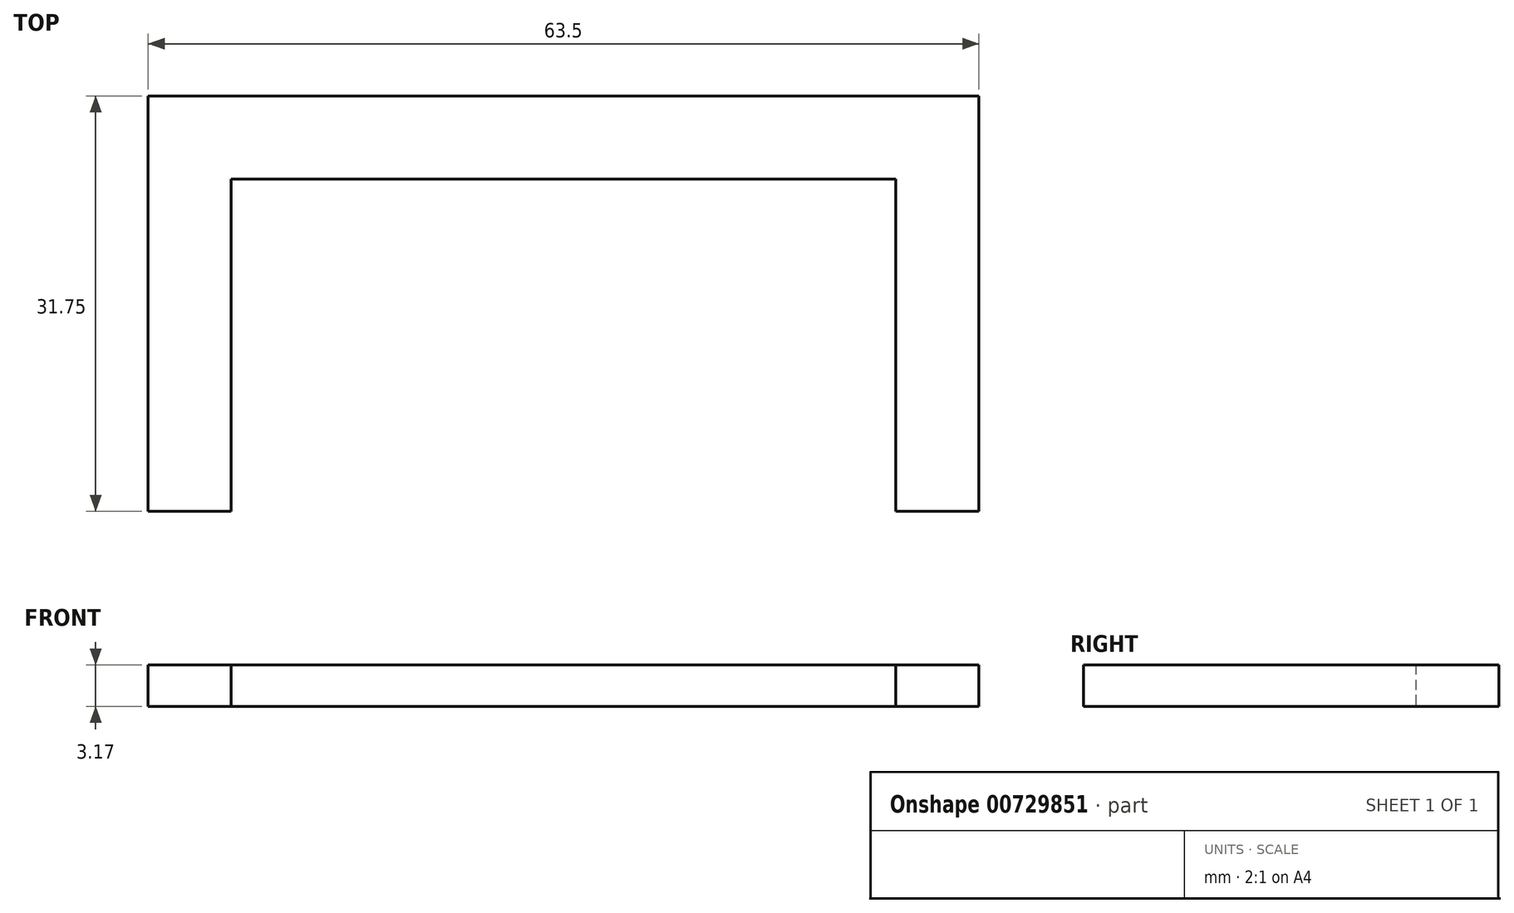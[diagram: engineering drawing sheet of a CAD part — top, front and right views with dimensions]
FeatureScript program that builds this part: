
annotation { "Feature Type Name" : "Feature", "Feature Type Description" : "" }
export const myFeature = defineFeature(function(context is Context, id is Id, definition is map)
    precondition{}
    {
        {
            var Q0;
            Q0=qCreatedBy(makeId("Top.planeOp"),FACE);
            var sketch = newSketch(context, id + "F0", { "sketchPlane" : qUnion([Q0])});
            skLineSegment(sketch, "E0", {"start": v(-85, -63.2) * mm, "end": v(-85, -31.44) * mm});
            skLineSegment(sketch, "E1", {"start": v(-85, -31.44) * mm, "end": v(-21.5, -31.44) * mm});
            skLineSegment(sketch, "E2", {"start": v(-21.5, -31.44) * mm, "end": v(-21.5, -63.2) * mm});
            skLineSegment(sketch, "E3", {"start": v(-78.65, -63.2) * mm, "end": v(-78.65, -37.8) * mm});
            skLineSegment(sketch, "E4", {"start": v(-27.85, -63.2) * mm, "end": v(-27.85, -37.8) * mm});
            skLineSegment(sketch, "E5", {"start": v(-78.65, -37.8) * mm, "end": v(-27.85, -37.8) * mm});
            skLineSegment(sketch, "E6", {"start": v(-27.85, -63.2) * mm, "end": v(-27.85, -31.44) * mm});
            skLineSegment(sketch, "E7", {"start": v(-85, -63.2) * mm, "end": v(-78.65, -63.2) * mm});
            skLineSegment(sketch, "E8", {"start": v(-27.85, -63.2) * mm, "end": v(-21.5, -63.2) * mm});
            skSolve(sketch);
        }
        {
            var Q0;
            {var subQ1=sQuery(id+"F0.wireOp",EDGE,"E0");Q0=makeQuery(id+"F0.imprint","IMPRINT",FACE,{"disambiguationData":[TD([[makeQuery(id+"F0.imprint","IMPRINT",EDGE,{"derivedFrom":subQ1}),-1.0]])]});}
            var Q1;
            {var subQ3=sQuery(id+"F0.wireOp",EDGE,"E2");Q1=makeQuery(id+"F0.imprint","IMPRINT",FACE,{"disambiguationData":[TD([[makeQuery(id+"F0.imprint","IMPRINT",EDGE,{"derivedFrom":subQ3}),-1.0]])]});}
            extrude(context, id + "F1", {"entities" : qUnion([Q0, Q1]), "depth" : 3.17 * mm, "offsetDistance" : 25.4 * mm});
        }
    });
